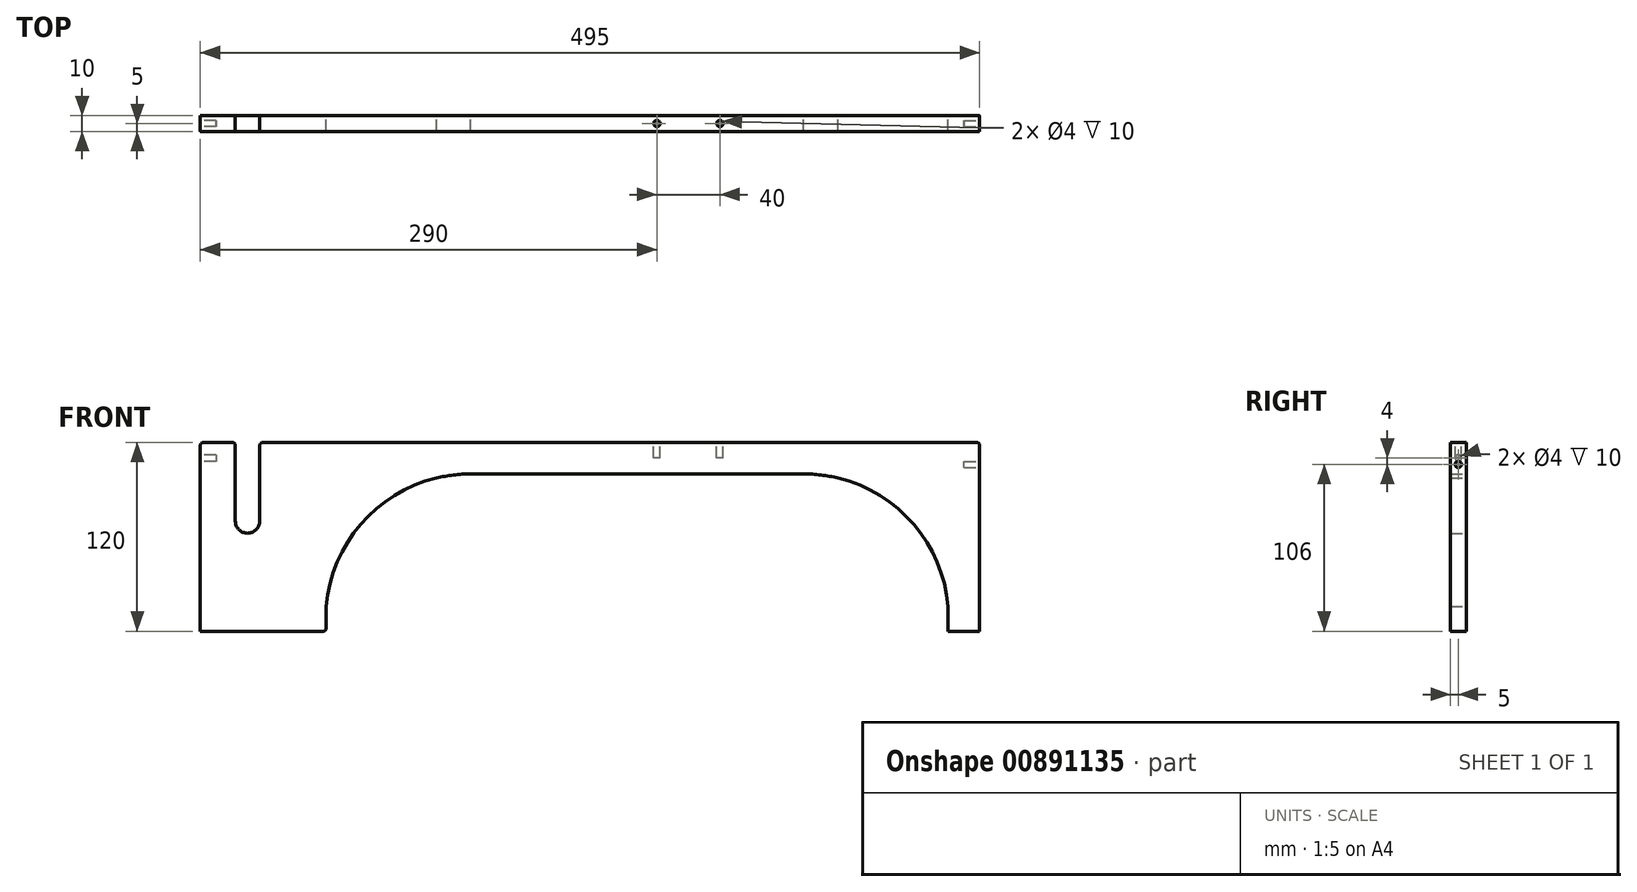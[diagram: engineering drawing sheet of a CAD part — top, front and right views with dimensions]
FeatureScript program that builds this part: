
annotation { "Feature Type Name" : "Feature", "Feature Type Description" : "" }
export const myFeature = defineFeature(function(context is Context, id is Id, definition is map)
    precondition{}
    {
        {
            var Q0;
            Q0=qCreatedBy(makeId("Front.planeOp"),FACE);
            var sketch = newSketch(context, id + "F0", { "sketchPlane" : qUnion([Q0])});
            skLineSegment(sketch, "E0.bottom", {"start": v(-277.5, -60) * mm, "end": v(-197.5, -60) * mm});
            skLineSegment(sketch, "E0.top", {"start": v(-277.5, 60) * mm, "end": v(-255.25, 60) * mm});
            skLineSegment(sketch, "E0.left", {"start": v(-277.5, -60) * mm, "end": v(-277.5, 60) * mm});
            skLineSegment(sketch, "E0.right", {"start": v(-197.5, -60) * mm, "end": v(-197.5, -44.17) * mm});
            skArc(sketch, "E1", {"start": v(-255.25, 10) * mm, "mid": v(-247.5, 2.25) * mm, "end": v(-239.75, 10) * mm});
            skLineSegment(sketch, "E2", {"start": v(-255.25, 10) * mm, "end": v(-255.25, 60) * mm});
            skLineSegment(sketch, "E3", {"start": v(-239.75, 10) * mm, "end": v(-239.75, 60) * mm});
            skLineSegment(sketch, "E4", {"start": v(217.5, 60) * mm, "end": v(217.5, 40) * mm});
            skLineSegment(sketch, "E5", {"start": v(105.76, 40) * mm, "end": v(-105.76, 40) * mm});
            skLineSegment(sketch, "E6", {"start": v(-239.75, 60) * mm, "end": v(217.5, 60) * mm});
            skLineSegment(sketch, "E7.top", {"start": v(217.5, -60) * mm, "end": v(197.5, -60) * mm});
            skLineSegment(sketch, "E7.left", {"start": v(217.5, 40) * mm, "end": v(217.5, -60) * mm});
            skLineSegment(sketch, "E7.right", {"start": v(197.5, -44.17) * mm, "end": v(197.5, -60) * mm});
            skArc(sketch, "E8", {"start": v(-105.76, 40) * mm, "mid": v(-116.74, 39.26) * mm, "end": v(-127.59, 37.38) * mm});
            skPoint(sketch, "E9.orphan", {"position": v(-197.5, 0) * mm});
            skArc(sketch, "E10", {"start": v(-127.59, 37.38) * mm, "mid": v(-175.66, 7.85) * mm, "end": v(-197.5, -44.17) * mm});
            skLineSegment(sketch, "E11", {"start": v(0, 0) * mm, "end": v(0, 252.37) * mm, "construction": true});
            skArc(sketch, "E12.MirrorCS", {"start": v(127.59, 37.38) * mm, "mid": v(175.66, 7.85) * mm, "end": v(197.5, -44.17) * mm});
            skArc(sketch, "E13.MirrorCS", {"start": v(105.76, 40) * mm, "mid": v(116.74, 39.26) * mm, "end": v(127.59, 37.38) * mm});
            skSolve(sketch);
        }
        {
            var Q0;
            Q0=qSketchRegion(id+"F0",true);
            extrude(context, id + "F1", {"entities" : qUnion([Q0]), "endBound" : BoundingType.SYMMETRIC, "depth" : 10 * mm, "offsetDistance" : 25 * mm});
        }
        {
            var Q0;
            Q0=makeQuery(id+"F1.opExtrude","SWEPT_EDGE",EDGE,{"disambiguationData":[OSD([sQuery(id+"F0.wireOp",EDGE,"E0.top"),sQuery(id+"F0.wireOp",EDGE,"E2")])]});
            var Q1;
            Q1=makeQuery(id+"F1.opExtrude","SWEPT_EDGE",EDGE,{"disambiguationData":[OSD([sQuery(id+"F0.wireOp",EDGE,"E3"),sQuery(id+"F0.wireOp",EDGE,"5932f437-94aa-491f-b3ef-b93f587fb4bc.trimOffspring")])]});
            var Q2;
            Q2=makeQuery(id+"F1.opExtrude","SWEPT_EDGE",EDGE,{"disambiguationData":[OSD([sQuery(id+"F0.wireOp",EDGE,"E0.right"),sQuery(id+"F0.wireOp",EDGE,"5932f437-94aa-491f-b3ef-b93f587fb4bc.trimOffspring")])]});
            var Q3;
            Q3=makeQuery(id+"F1.opExtrude","SWEPT_EDGE",EDGE,{"disambiguationData":[OSD([sQuery(id+"F0.wireOp",EDGE,"E0.top"),sQuery(id+"F0.wireOp",EDGE,"E0.left")])]});
            fillet(context, id + "F2", {"entities" : qUnion([Q0, Q1, Q2, Q3]), "radius" : 2 * mm, "tangentPropagation" : true, "allowEdgeOverflow" : false});
        }
        {
            var Q0;
            Q0=makeQuery(id+"F1.opExtrude","SWEPT_EDGE",EDGE,{"disambiguationData":[OSD([sQuery(id+"F0.wireOp",EDGE,"E4"),sQuery(id+"F0.wireOp",EDGE,"E6")])]});
            fillet(context, id + "F3", {"entities" : qUnion([Q0]), "radius" : 2 * mm, "tangentPropagation" : true, "allowEdgeOverflow" : false});
        }
        {
            var Q0;
            Q0=makeQuery(id+"F1.opExtrude","SWEPT_FACE",FACE,{"disambiguationData":[OSD([sQuery(id+"F0.wireOp",EDGE,"E6")])]});
            var sketch = newSketch(context, id + "F4", { "sketchPlane" : qUnion([Q0])});
            skCircle(sketch, "E14", {"center": v(12.5, 0) * mm, "radius": 2 * mm});
            skLineSegment(sketch, "E15", {"start": v(32.5, 58.93) * mm, "end": v(32.5, -35.44) * mm, "construction": true});
            skCircle(sketch, "E16.MirrorC", {"center": v(52.5, 0) * mm, "radius": 2 * mm});
            skSolve(sketch);
        }
        {
            var Q0;
            Q0 = qSketchRegion(id + "F4", true);
            extrude(context, id + "F5", {"entities" : qUnion([Q0]), "operationType" : NewBodyOperationType.REMOVE, "oppositeDirection" : true, "depth" : 10 * mm, "offsetDistance" : 25 * mm});
        }
        {
            var Q0;
            Q0=makeQuery(id+"F1.opExtrude","SWEPT_FACE",FACE,{"disambiguationData":[OSD([sQuery(id+"F0.wireOp",EDGE,"E4"),sQuery(id+"F0.wireOp",EDGE,"E7.left")])]});
            var sketch = newSketch(context, id + "F6", { "sketchPlane" : qUnion([Q0])});
            skCircle(sketch, "E17", {"center": v(0, 46) * mm, "radius": 2 * mm});
            skSolve(sketch);
        }
        {
            var Q0;
            Q0 = qSketchRegion(id + "F6", true);
            extrude(context, id + "F7", {"entities" : qUnion([Q0]), "operationType" : NewBodyOperationType.REMOVE, "oppositeDirection" : true, "depth" : 10 * mm, "offsetDistance" : 25 * mm});
        }
        {
            var Q0;
            Q0=makeQuery(id+"F1.opExtrude","SWEPT_FACE",FACE,{"disambiguationData":[OSD([sQuery(id+"F0.wireOp",EDGE,"E0.left")])]});
            var sketch = newSketch(context, id + "F8", { "sketchPlane" : qUnion([Q0])});
            skCircle(sketch, "E18", {"center": v(0, 50) * mm, "radius": 2 * mm});
            skSolve(sketch);
        }
        {
            var Q0;
            Q0 = qSketchRegion(id + "F8", true);
            extrude(context, id + "F9", {"entities" : qUnion([Q0]), "operationType" : NewBodyOperationType.REMOVE, "oppositeDirection" : true, "depth" : 10 * mm, "offsetDistance" : 25 * mm});
        }
    });
